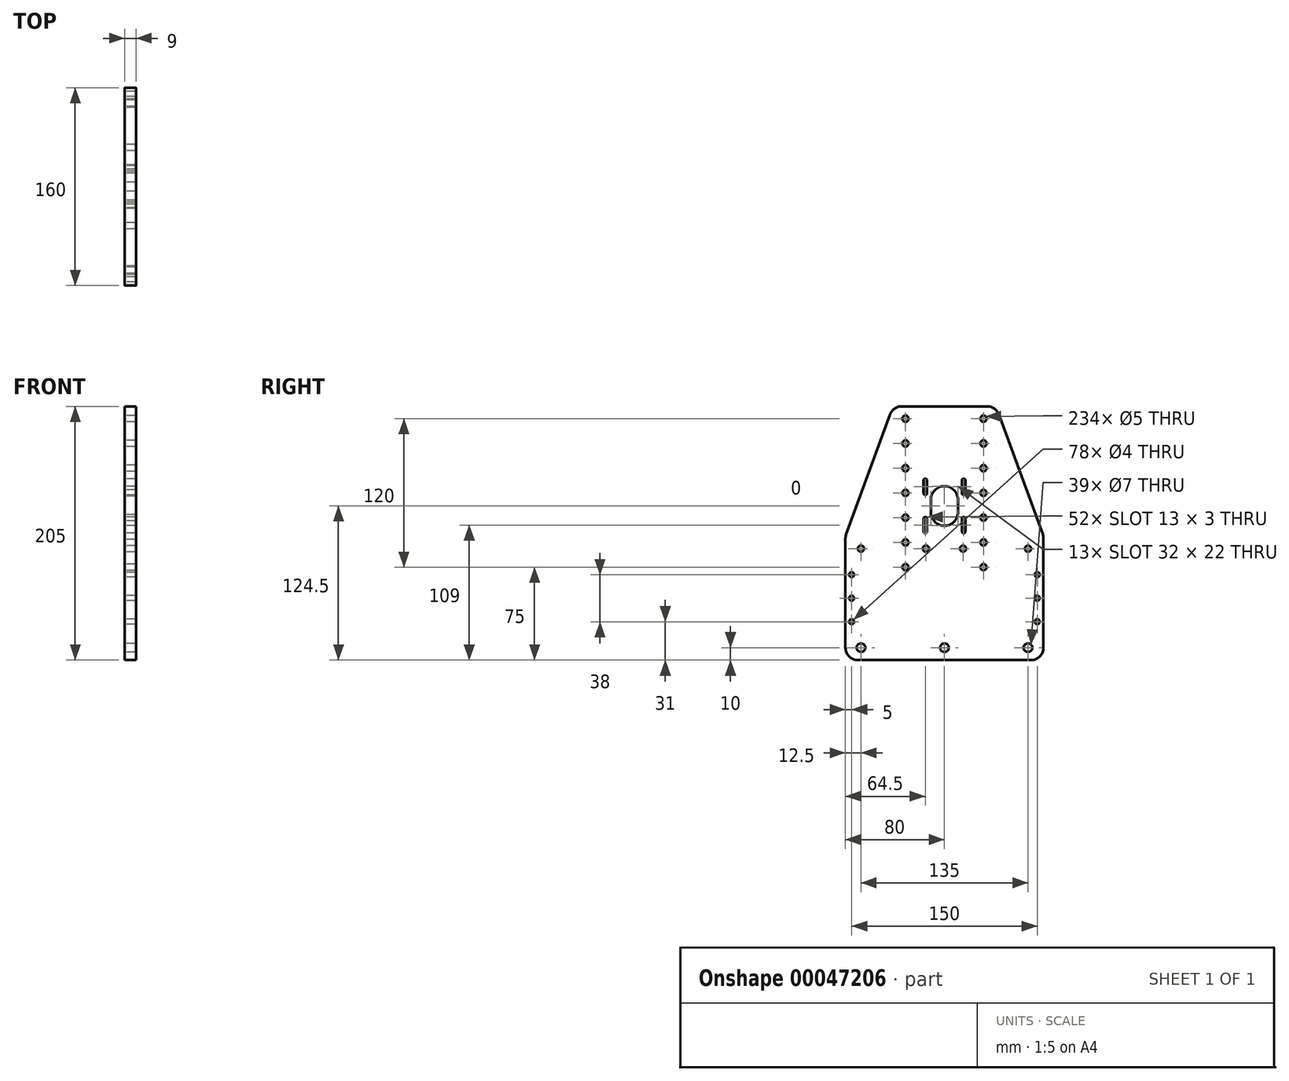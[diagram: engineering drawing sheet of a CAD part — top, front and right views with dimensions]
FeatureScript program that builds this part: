
annotation { "Feature Type Name" : "Feature", "Feature Type Description" : "" }
export const myFeature = defineFeature(function(context is Context, id is Id, definition is map)
    precondition{}
    {
        {
            var Q0;
            Q0=qCreatedBy(makeId("Right.planeOp"),FACE);
            var sketch = newSketch(context, id + "F0", { "sketchPlane" : qUnion([Q0])});
            skLineSegment(sketch, "E0.bottom", {"start": v(-34.52, 205) * mm, "end": v(34.52, 205) * mm});
            skLineSegment(sketch, "E0.top", {"start": v(-70, 0) * mm, "end": v(70, 0) * mm});
            skLineSegment(sketch, "E0.left", {"start": v(-80, 98.22) * mm, "end": v(-80, 10) * mm});
            skCircle(sketch, "E1", {"center": v(-67.5, 10) * mm, "radius": 3.5 * mm});
            skCircle(sketch, "E2.MirrorC", {"center": v(67.5, 10) * mm, "radius": 3.5 * mm});
            skCircle(sketch, "E3", {"center": v(-67.5, 90) * mm, "radius": 2.5 * mm});
            skCircle(sketch, "E4.MirrorC", {"center": v(67.5, 90) * mm, "radius": 2.5 * mm});
            skCircle(sketch, "E5", {"center": v(-15, 90) * mm, "radius": 2.5 * mm});
            skCircle(sketch, "E6.MirrorC", {"center": v(15, 90) * mm, "radius": 2.5 * mm});
            skArc(sketch, "E7", {"start": v(-14, 145) * mm, "mid": v(-15.5, 146.5) * mm, "end": v(-17, 145) * mm});
            skArc(sketch, "E8", {"start": v(-17, 135) * mm, "mid": v(-15.5, 133.5) * mm, "end": v(-14, 135) * mm});
            skCircle(sketch, "E9", {"center": v(-31.5, 195) * mm, "radius": 2.5 * mm});
            skCircle(sketch, "E10", {"center": v(-31.5, 155) * mm, "radius": 2.5 * mm});
            skLineSegment(sketch, "E11", {"start": v(-17, 145) * mm, "end": v(-17, 135) * mm});
            skArc(sketch, "E12", {"start": v(-17, 104) * mm, "mid": v(-15.5, 102.5) * mm, "end": v(-14, 104) * mm});
            skArc(sketch, "E13", {"start": v(-14, 114) * mm, "mid": v(-15.5, 115.5) * mm, "end": v(-17, 114) * mm});
            skLineSegment(sketch, "E14", {"start": v(-17, 114) * mm, "end": v(-17, 104) * mm});
            skCircle(sketch, "E15.MirrorC", {"center": v(31.5, 195) * mm, "radius": 2.5 * mm});
            skCircle(sketch, "E16.MirrorC", {"center": v(31.5, 155) * mm, "radius": 2.5 * mm});
            skLineSegment(sketch, "E17", {"start": v(-15.5, 114) * mm, "end": v(-15.5, 104) * mm, "construction": true});
            skLineSegment(sketch, "E18.MirrorCS", {"start": v(-14, 114) * mm, "end": v(-14, 104) * mm});
            skArc(sketch, "E19.MirrorCS", {"start": v(-14, 104) * mm, "mid": v(-15.5, 102.5) * mm, "end": v(-17, 104) * mm});
            skArc(sketch, "E20.MirrorCS", {"start": v(-17, 114) * mm, "mid": v(-15.5, 115.5) * mm, "end": v(-14, 114) * mm});
            skArc(sketch, "E21.MirrorCS", {"start": v(17, 104) * mm, "mid": v(15.5, 102.5) * mm, "end": v(14, 104) * mm});
            skLineSegment(sketch, "E22.MirrorCS", {"start": v(17, 114) * mm, "end": v(17, 104) * mm});
            skArc(sketch, "E23.MirrorCS", {"start": v(14, 114) * mm, "mid": v(15.5, 115.5) * mm, "end": v(17, 114) * mm});
            skLineSegment(sketch, "E24.MirrorCS", {"start": v(14, 114) * mm, "end": v(14, 104) * mm});
            skArc(sketch, "E25.MirrorCS", {"start": v(17, 114) * mm, "mid": v(15.5, 115.5) * mm, "end": v(14, 114) * mm});
            skLineSegment(sketch, "E26.MirrorCS", {"start": v(15.5, 114) * mm, "end": v(15.5, 104) * mm, "construction": true});
            skArc(sketch, "E27.MirrorCS", {"start": v(14, 104) * mm, "mid": v(15.5, 102.5) * mm, "end": v(17, 104) * mm});
            skLineSegment(sketch, "E28", {"start": v(-15.5, 145) * mm, "end": v(-15.5, 135) * mm, "construction": true});
            skLineSegment(sketch, "E29.MirrorCS", {"start": v(-14, 145) * mm, "end": v(-14, 135) * mm});
            skLineSegment(sketch, "E30.MirrorCS", {"start": v(14, 145) * mm, "end": v(14, 135) * mm});
            skLineSegment(sketch, "E31.MirrorCS", {"start": v(17, 145) * mm, "end": v(17, 135) * mm});
            skLineSegment(sketch, "E32.MirrorCS", {"start": v(15.5, 145) * mm, "end": v(15.5, 135) * mm, "construction": true});
            skArc(sketch, "E33.MirrorCS", {"start": v(17, 135) * mm, "mid": v(15.5, 133.5) * mm, "end": v(14, 135) * mm});
            skArc(sketch, "E34.MirrorCS", {"start": v(14, 145) * mm, "mid": v(15.5, 146.5) * mm, "end": v(17, 145) * mm});
            skLineSegment(sketch, "E35.MirrorCS", {"start": v(80, 98.22) * mm, "end": v(80, 10) * mm});
            skPoint(sketch, "E36.visualSharp", {"position": v(-80, 0) * mm});
            skArc(sketch, "E36.filletArc", {"start": v(-80, 10) * mm, "mid": v(-77.07, 2.93) * mm, "end": v(-70, 0) * mm});
            skPoint(sketch, "E37.visualSharp", {"position": v(80, 0) * mm});
            skArc(sketch, "E37.filletArc", {"start": v(70, 0) * mm, "mid": v(77.07, 2.93) * mm, "end": v(80, 10) * mm});
            skCircle(sketch, "E38", {"center": v(0, 10) * mm, "radius": 3.5 * mm});
            skLineSegment(sketch, "E39", {"start": v(-43.9, 198.44) * mm, "end": v(-79.39, 101.67) * mm});
            skLineSegment(sketch, "E40.MirrorCS", {"start": v(43.9, 198.44) * mm, "end": v(79.39, 101.67) * mm});
            skPoint(sketch, "E41.visualSharp", {"position": v(-41.5, 205) * mm});
            skArc(sketch, "E41.filletArc", {"start": v(-34.52, 205) * mm, "mid": v(-40.24, 203.2) * mm, "end": v(-43.9, 198.44) * mm});
            skPoint(sketch, "E42.visualSharp", {"position": v(41.5, 205) * mm});
            skArc(sketch, "E42.filletArc", {"start": v(43.9, 198.44) * mm, "mid": v(40.24, 203.2) * mm, "end": v(34.52, 205) * mm});
            skPoint(sketch, "E43.visualSharp", {"position": v(-80, 100) * mm});
            skArc(sketch, "E43.filletArc", {"start": v(-79.39, 101.67) * mm, "mid": v(-79.85, 99.97) * mm, "end": v(-80, 98.22) * mm});
            skPoint(sketch, "E44.visualSharp", {"position": v(80, 100) * mm});
            skArc(sketch, "E44.filletArc", {"start": v(80, 98.22) * mm, "mid": v(79.85, 99.97) * mm, "end": v(79.39, 101.67) * mm});
            skArc(sketch, "E45", {"start": v(11, 129.5) * mm, "mid": v(0, 140.5) * mm, "end": v(-11, 129.5) * mm});
            skArc(sketch, "E46", {"start": v(-11, 119.5) * mm, "mid": v(0, 108.5) * mm, "end": v(11, 119.5) * mm});
            skLineSegment(sketch, "E47", {"start": v(-11, 129.5) * mm, "end": v(-11, 119.5) * mm});
            skLineSegment(sketch, "E48", {"start": v(11, 129.5) * mm, "end": v(11, 119.5) * mm});
            skCircle(sketch, "E49", {"center": v(-75, 69) * mm, "radius": 2 * mm});
            skCircle(sketch, "E50", {"center": v(-75, 50) * mm, "radius": 2 * mm});
            skCircle(sketch, "E51", {"center": v(-75, 31) * mm, "radius": 2 * mm});
            skCircle(sketch, "E52.MirrorC", {"center": v(75, 31) * mm, "radius": 2 * mm});
            skCircle(sketch, "E53.MirrorC", {"center": v(75, 50) * mm, "radius": 2 * mm});
            skCircle(sketch, "E54.MirrorC", {"center": v(75, 69) * mm, "radius": 2 * mm});
            skCircle(sketch, "E55", {"center": v(-31.5, 175) * mm, "radius": 2.5 * mm});
            skCircle(sketch, "E56.MirrorC", {"center": v(31.5, 175) * mm, "radius": 2.5 * mm});
            skLineSegment(sketch, "E57", {"start": v(-31.5, 155) * mm, "end": v(31.5, 155) * mm, "construction": true});
            skCircle(sketch, "E58.MirrorC", {"center": v(-31.5, 135) * mm, "radius": 2.5 * mm});
            skCircle(sketch, "E59.MirrorC", {"center": v(31.5, 135) * mm, "radius": 2.5 * mm});
            skCircle(sketch, "E60.MirrorC", {"center": v(-31.5, 115) * mm, "radius": 2.5 * mm});
            skCircle(sketch, "E61.MirrorC", {"center": v(31.5, 115) * mm, "radius": 2.5 * mm});
            skLineSegment(sketch, "E62", {"start": v(-31.5, 115) * mm, "end": v(31.5, 115) * mm, "construction": true});
            skCircle(sketch, "E63.MirrorC", {"center": v(-31.5, 95) * mm, "radius": 2.5 * mm});
            skCircle(sketch, "E64.MirrorC", {"center": v(31.5, 95) * mm, "radius": 2.5 * mm});
            skCircle(sketch, "E65.MirrorC", {"center": v(-31.5, 75) * mm, "radius": 2.5 * mm});
            skCircle(sketch, "E66.MirrorC", {"center": v(31.5, 75) * mm, "radius": 2.5 * mm});
            skSolve(sketch);
        }
        {
            var Q0;
            Q0=makeQuery(id+"F0.imprint","IMPRINT",FACE,{"disambiguationData":[TD([[makeQuery(id+"F0.imprint","IMPRINT",EDGE,{"derivedFrom":sQuery(id+"F0.wireOp",EDGE,"E0.bottom")}),-1.0]])]});
            extrude(context, id + "F1", {"entities" : qUnion([Q0]), "depth" : 9 * mm});
        }
    });
